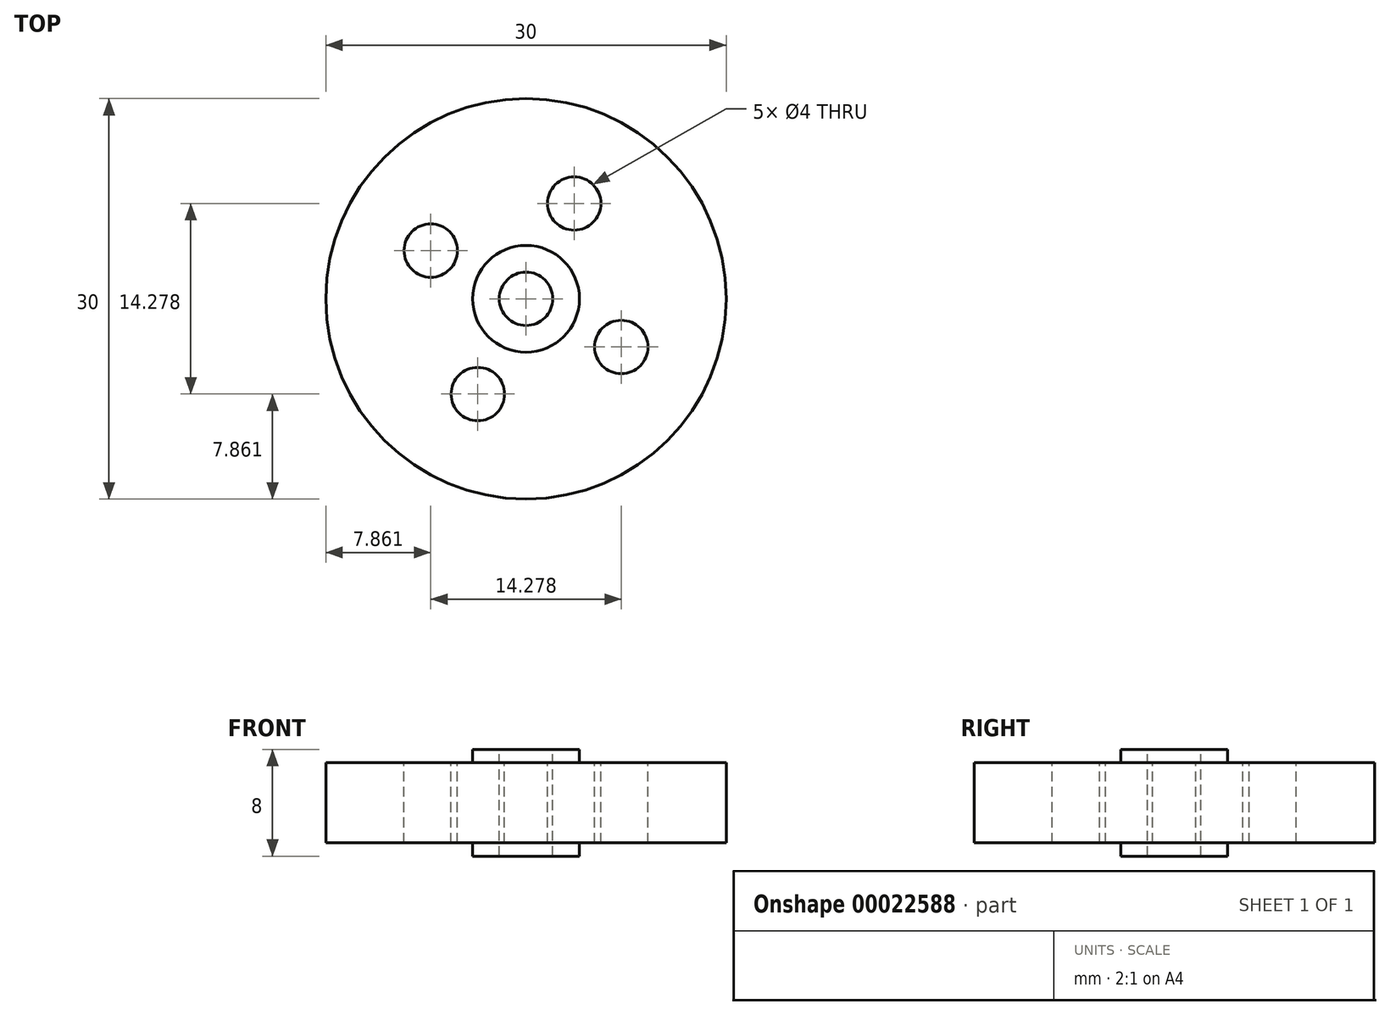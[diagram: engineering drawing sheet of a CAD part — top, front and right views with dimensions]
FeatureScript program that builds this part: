
annotation { "Feature Type Name" : "Feature", "Feature Type Description" : "" }
export const myFeature = defineFeature(function(context is Context, id is Id, definition is map)
    precondition{}
    {
        {
            var Q0;
            Q0=qCreatedBy(makeId("Top.planeOp"),FACE);
            var sketch = newSketch(context, id + "F0", { "sketchPlane" : qUnion([Q0])});
            skCircle(sketch, "E0", {"center": v(0, 0) * mm, "radius": 15 * mm});
            skSolve(sketch);
        }
        {
            var Q0;
            Q0=makeQuery(id+"F0.imprint","IMPRINT",FACE,{"disambiguationData":[TD([[makeQuery(id+"F0.imprint","IMPRINT",EDGE,{"derivedFrom":sQuery(id+"F0.wireOp",EDGE,"E0")}),1.0]])]});
            var Q1;
            Q1=sQuery(id+"F0.wireOp",EDGE,"E0");
            extrude(context, id + "F1", {"entities" : qUnion([Q0]), "surfaceEntities" : qUnion([Q1]), "depth" : 6 * mm});
        }
        {
            var Q0;
            Q0=makeQuery(id+"F1.opExtrude","CAP_FACE",FACE,{"disambiguationData":[OSD([sQuery(id+"F0.wireOp",EDGE,"E0")])],"isStart":false});
            var sketch = newSketch(context, id + "F2", { "sketchPlane" : qUnion([Q0])});
            skCircle(sketch, "E1", {"center": v(0, 0) * mm, "radius": 4 * mm});
            skCircle(sketch, "E2", {"center": v(0, 0) * mm, "radius": 2 * mm});
            skCircle(sketch, "E3", {"center": v(-7.14, 3.61) * mm, "radius": 2 * mm});
            skCircle(sketch, "E4.1.0", {"center": v(-3.61, -7.14) * mm, "radius": 2 * mm});
            skCircle(sketch, "E4.2.0", {"center": v(7.14, -3.61) * mm, "radius": 2 * mm});
            skCircle(sketch, "E4.3.0", {"center": v(3.61, 7.14) * mm, "radius": 2 * mm});
            skSolve(sketch);
        }
        {
            var Q0;
            Q0=makeQuery(id+"F2.imprint","IMPRINT",FACE,{"disambiguationData":[TD([[makeQuery(id+"F2.imprint","IMPRINT",EDGE,{"derivedFrom":sQuery(id+"F2.wireOp",EDGE,"E3")}),1.0]])]});
            var Q1;
            Q1=makeQuery(id+"F2.imprint","IMPRINT",FACE,{"disambiguationData":[TD([[makeQuery(id+"F2.imprint","IMPRINT",EDGE,{"derivedFrom":sQuery(id+"F2.wireOp",EDGE,"E4.3.0")}),1.0]])]});
            var Q2;
            Q2=makeQuery(id+"F2.imprint","IMPRINT",FACE,{"disambiguationData":[TD([[makeQuery(id+"F2.imprint","IMPRINT",EDGE,{"derivedFrom":sQuery(id+"F2.wireOp",EDGE,"E4.2.0")}),1.0]])]});
            var Q3;
            Q3=makeQuery(id+"F2.imprint","IMPRINT",FACE,{"disambiguationData":[TD([[makeQuery(id+"F2.imprint","IMPRINT",EDGE,{"derivedFrom":sQuery(id+"F2.wireOp",EDGE,"E4.1.0")}),1.0]])]});
            var Q4;
            Q4=makeQuery(id+"F2.imprint","IMPRINT",FACE,{"disambiguationData":[TD([[makeQuery(id+"F2.imprint","IMPRINT",EDGE,{"derivedFrom":sQuery(id+"F2.wireOp",EDGE,"E2")}),1.0]])]});
            extrude(context, id + "F3", {"entities" : qUnion([Q0, Q1, Q2, Q3, Q4]), "operationType" : NewBodyOperationType.REMOVE, "endBound" : BoundingType.THROUGH_ALL, "oppositeDirection" : true, "depth" : 25.4 * mm});
        }
        {
            var Q0;
            Q0=makeQuery(id+"F2.imprint","IMPRINT",FACE,{"disambiguationData":[TD([[makeQuery(id+"F2.imprint","IMPRINT",EDGE,{"derivedFrom":sQuery(id+"F2.wireOp",EDGE,"E1")}),1.0]])]});
            extrude(context, id + "F4", {"entities" : qUnion([Q0]), "operationType" : NewBodyOperationType.ADD, "depth" : 1 * mm});
        }
        {
            var Q0;
            Q0=makeQuery(id+"F1.opExtrude","CAP_FACE",FACE,{"disambiguationData":[OSD([sQuery(id+"F0.wireOp",EDGE,"E0")])],"isStart":true});
            var sketch = newSketch(context, id + "F5", { "sketchPlane" : qUnion([Q0])});
            skCircle(sketch, "E5", {"center": v(0, 0) * mm, "radius": 4 * mm});
            skSolve(sketch);
        }
        {
            var Q0;
            Q0=makeQuery(id+"F5.imprint","IMPRINT",FACE,{"disambiguationData":[TD([[makeQuery(id+"F5.imprint","IMPRINT",EDGE,{"derivedFrom":sQuery(id+"F5.wireOp",EDGE,"E5")}),1.0]])]});
            extrude(context, id + "F6", {"entities" : qUnion([Q0]), "operationType" : NewBodyOperationType.ADD, "depth" : 1 * mm});
        }
    });
